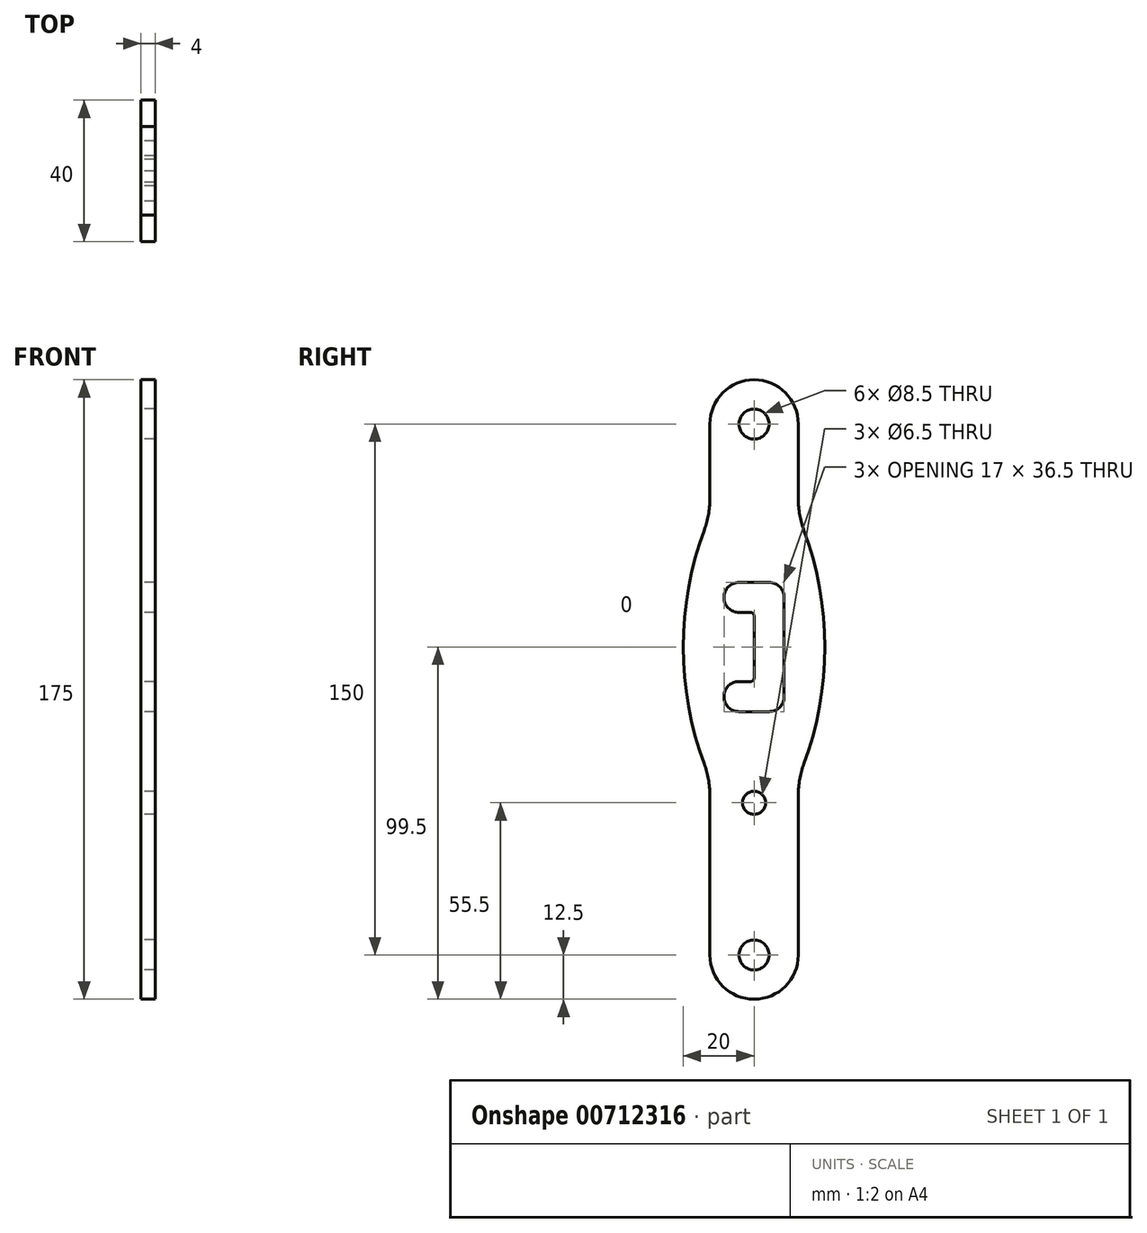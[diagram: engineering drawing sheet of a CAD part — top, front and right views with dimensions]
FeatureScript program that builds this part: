
annotation { "Feature Type Name" : "Feature", "Feature Type Description" : "" }
export const myFeature = defineFeature(function(context is Context, id is Id, definition is map)
    precondition{}
    {
        {
            var Q0;
            Q0=qCreatedBy(makeId("Right.planeOp"),FACE);
            var sketch = newSketch(context, id + "F0", { "sketchPlane" : qUnion([Q0])});
            skLineSegment(sketch, "E0.bottom", {"start": v(12.5, 0) * mm, "end": v(-12.5, 0) * mm, "construction": true});
            skLineSegment(sketch, "E0.top", {"start": v(12.5, 150) * mm, "end": v(-12.5, 150) * mm, "construction": true});
            skLineSegment(sketch, "E0.left", {"start": v(12.5, 0) * mm, "end": v(12.5, 50) * mm});
            skLineSegment(sketch, "E0.right", {"start": v(-12.5, 0) * mm, "end": v(-12.5, 50) * mm});
            skArc(sketch, "E1", {"start": v(12.5, 150) * mm, "mid": v(0, 162.5) * mm, "end": v(-12.5, 150) * mm});
            skArc(sketch, "E2", {"start": v(-12.5, 0) * mm, "mid": v(0, -12.5) * mm, "end": v(12.5, 0) * mm});
            skCircle(sketch, "E3", {"center": v(0, 0) * mm, "radius": 4.25 * mm});
            skCircle(sketch, "E4", {"center": v(0, 150) * mm, "radius": 4.25 * mm});
            skPoint(sketch, "E5", {"position": v(12.5, 75) * mm});
            skLineSegment(sketch, "E6.bottom", {"start": v(-4.25, 105.25) * mm, "end": v(4.25, 105.25) * mm});
            skLineSegment(sketch, "E6.top", {"start": v(-4.25, 68.75) * mm, "end": v(4.25, 68.75) * mm});
            skLineSegment(sketch, "E6.right", {"start": v(8.5, 101) * mm, "end": v(8.5, 73) * mm});
            skLineSegment(sketch, "E7", {"start": v(0, 150) * mm, "end": v(0, 0) * mm, "construction": true});
            skPoint(sketch, "E8.visualSharp", {"position": v(8.5, 105.25) * mm});
            skArc(sketch, "E8.filletArc", {"start": v(8.5, 101) * mm, "mid": v(7.26, 104) * mm, "end": v(4.25, 105.25) * mm});
            skPoint(sketch, "E9.visualSharp", {"position": v(8.5, 68.75) * mm});
            skArc(sketch, "E9.filletArc", {"start": v(4.25, 68.75) * mm, "mid": v(7.26, 70) * mm, "end": v(8.5, 73) * mm});
            skLineSegment(sketch, "E10", {"start": v(-4.25, 96.75) * mm, "end": v(0, 96.75) * mm});
            skLineSegment(sketch, "E11", {"start": v(0, 96.75) * mm, "end": v(0, 77.25) * mm});
            skLineSegment(sketch, "E12", {"start": v(0, 77.25) * mm, "end": v(-4.25, 77.25) * mm});
            skArc(sketch, "E13", {"start": v(-4.25, 77.25) * mm, "mid": v(-8.5, 73) * mm, "end": v(-4.25, 68.75) * mm});
            skArc(sketch, "E14", {"start": v(-4.25, 68.75) * mm, "mid": v(0, 73) * mm, "end": v(-4.25, 77.25) * mm, "construction": true});
            skArc(sketch, "E15", {"start": v(-4.25, 105.25) * mm, "mid": v(-8.5, 101) * mm, "end": v(-4.25, 96.75) * mm});
            skArc(sketch, "E16", {"start": v(-4.25, 96.75) * mm, "mid": v(0, 101) * mm, "end": v(-4.25, 105.25) * mm, "construction": true});
            skCircle(sketch, "E17", {"center": v(0, 43) * mm, "radius": 3.25 * mm});
            skPoint(sketch, "E18", {"position": v(8.5, 87) * mm});
            skLineSegment(sketch, "E19", {"start": v(-75, 87) * mm, "end": v(75, 87) * mm, "construction": true});
            skPoint(sketch, "E19.startSnap0", {"position": v(0, 87) * mm});
            skPoint(sketch, "E19.endSnap0", {"position": v(0, 87) * mm});
            skLineSegment(sketch, "E20", {"start": v(12.5, 124) * mm, "end": v(12.5, 124) * mm});
            skArc(sketch, "E21", {"start": v(-12.5, 124) * mm, "mid": v(-20, 87) * mm, "end": v(-12.5, 50) * mm});
            skLineSegment(sketch, "E22", {"start": v(-12.5, 124) * mm, "end": v(-12.5, 150) * mm});
            skLineSegment(sketch, "E23", {"start": v(-12.5, 50) * mm, "end": v(-12.5, 124) * mm, "construction": true});
            skArc(sketch, "E24", {"start": v(12.5, 124) * mm, "mid": v(20, 87) * mm, "end": v(12.5, 50) * mm});
            skLineSegment(sketch, "E25", {"start": v(12.5, 50) * mm, "end": v(12.5, 50) * mm});
            skLineSegment(sketch, "E26", {"start": v(12.5, 124) * mm, "end": v(12.5, 150) * mm});
            skLineSegment(sketch, "E27", {"start": v(12.5, 50) * mm, "end": v(12.5, 124) * mm, "construction": true});
            skSolve(sketch);
        }
        {
            var Q0;
            Q0 = qSketchRegion(id + "F0", true);
            extrude(context, id + "F1", {"entities" : qUnion([Q0]), "depth" : 4 * mm, "offsetDistance" : 25 * mm});
        }
        {
            var Q0;
            Q0=makeQuery(id+"F1.opExtrude","SWEPT_EDGE",EDGE,{"disambiguationData":[OSD([sQuery(id+"F0.wireOp",EDGE,"E24"),sQuery(id+"F0.wireOp",EDGE,"E26")])]});
            var Q1;
            Q1=makeQuery(id+"F1.opExtrude","SWEPT_EDGE",EDGE,{"disambiguationData":[OSD([sQuery(id+"F0.wireOp",EDGE,"E21"),sQuery(id+"F0.wireOp",EDGE,"E22")])]});
            var Q2;
            Q2=makeQuery(id+"F1.opExtrude","SWEPT_EDGE",EDGE,{"disambiguationData":[OSD([sQuery(id+"F0.wireOp",EDGE,"E0.right"),sQuery(id+"F0.wireOp",EDGE,"E21")])]});
            var Q3;
            Q3=makeQuery(id+"F1.opExtrude","SWEPT_EDGE",EDGE,{"disambiguationData":[OSD([sQuery(id+"F0.wireOp",EDGE,"E0.left"),sQuery(id+"F0.wireOp",EDGE,"E24")])]});
            fillet(context, id + "F2", {"entities" : qUnion([Q0, Q1, Q2, Q3]), "radius" : 25 * mm, "tangentPropagation" : true, "allowEdgeOverflow" : false});
        }
        {
            var Q0;
            Q0=makeQuery(id+"F1.opExtrude","SWEPT_EDGE",EDGE,{"disambiguationData":[OSD([sQuery(id+"F0.wireOp",EDGE,"E10"),sQuery(id+"F0.wireOp",EDGE,"E11")])]});
            var Q1;
            Q1=makeQuery(id+"F1.opExtrude","SWEPT_EDGE",EDGE,{"disambiguationData":[OSD([sQuery(id+"F0.wireOp",EDGE,"E11"),sQuery(id+"F0.wireOp",EDGE,"E12")])]});
            fillet(context, id + "F3", {"entities" : qUnion([Q0, Q1]), "radius" : 1 * mm, "tangentPropagation" : true, "allowEdgeOverflow" : false});
        }
    });
